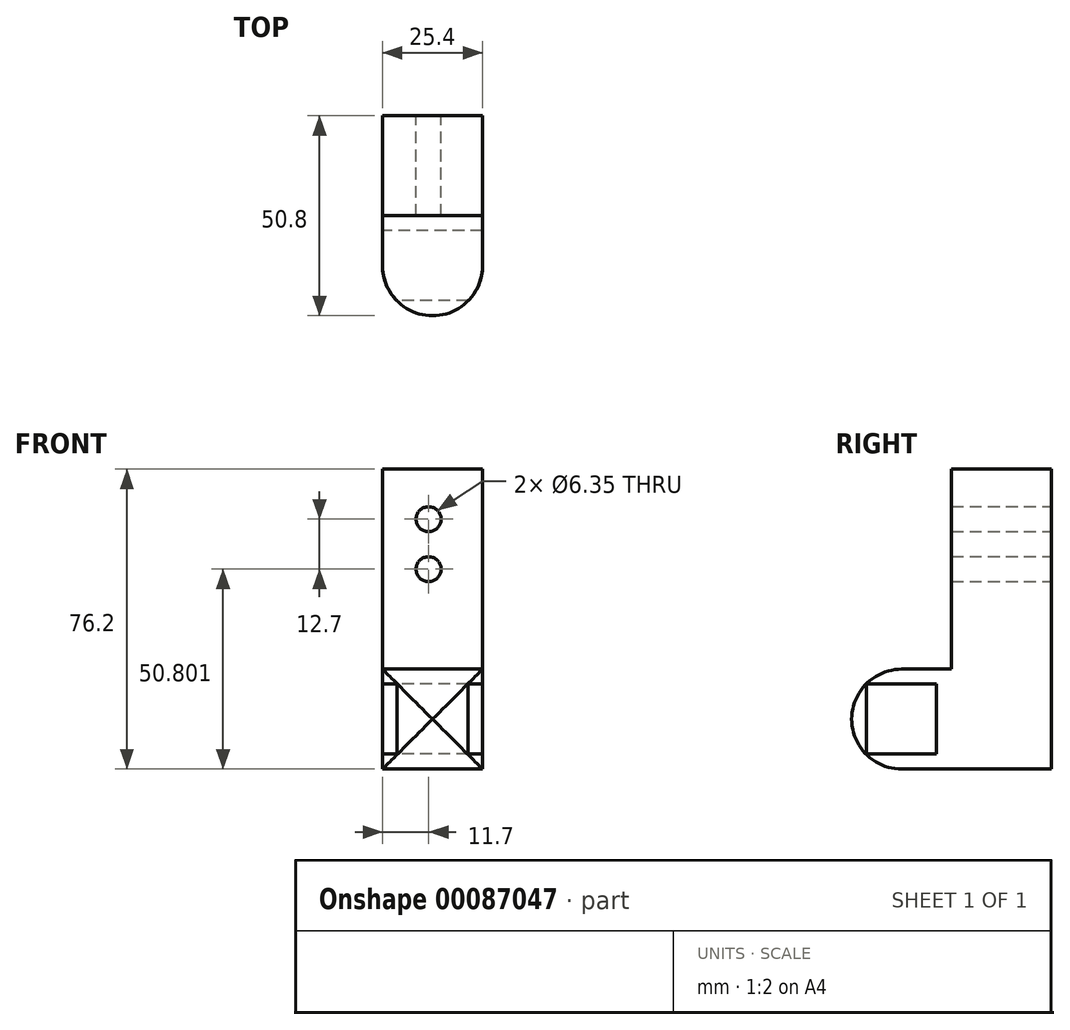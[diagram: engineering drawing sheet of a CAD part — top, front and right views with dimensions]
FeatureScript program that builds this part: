
annotation { "Feature Type Name" : "Feature", "Feature Type Description" : "" }
export const myFeature = defineFeature(function(context is Context, id is Id, definition is map)
    precondition{}
    {
        {
            var Q0;
            Q0=qCreatedBy(makeId("Front.planeOp"),FACE);
            var sketch = newSketch(context, id + "F0", { "sketchPlane" : qUnion([Q0])});
            skLineSegment(sketch, "E0.bottom", {"start": v(-11.7, 54.66) * mm, "end": v(13.7, 54.66) * mm});
            skLineSegment(sketch, "E0.top", {"start": v(-11.7, -21.54) * mm, "end": v(13.7, -21.54) * mm});
            skLineSegment(sketch, "E0.left", {"start": v(-11.7, 54.66) * mm, "end": v(-11.7, -21.54) * mm});
            skLineSegment(sketch, "E0.right", {"start": v(13.7, 54.66) * mm, "end": v(13.7, -21.54) * mm});
            skCircle(sketch, "E1", {"center": v(0, 41.96) * mm, "radius": 3.18 * mm});
            skCircle(sketch, "E2", {"center": v(0, 29.26) * mm, "radius": 3.18 * mm});
            skSolve(sketch);
        }
        {
            var Q0;
            Q0=makeQuery(id+"F0.imprint","IMPRINT",FACE,{"disambiguationData":[TD([[makeQuery(id+"F0.imprint","IMPRINT",EDGE,{"derivedFrom":sQuery(id+"F0.wireOp",EDGE,"E0.bottom")}),-1.0]])]});
            extrude(context, id + "F1", {"entities" : qUnion([Q0]), "depth" : 25.4 * mm});
        }
        {
            var Q0;
            Q0=makeQuery(id+"F1.opExtrude","CAP_FACE",FACE,{"disambiguationData":[OSD([sQuery(id+"F0.wireOp",EDGE,"E0.bottom"),sQuery(id+"F0.wireOp",EDGE,"E0.top"),sQuery(id+"F0.wireOp",EDGE,"E0.left"),sQuery(id+"F0.wireOp",EDGE,"E0.right"),sQuery(id+"F0.wireOp",EDGE,"E1"),sQuery(id+"F0.wireOp",EDGE,"E2")])],"isStart":false});
            var sketch = newSketch(context, id + "F2", { "sketchPlane" : qUnion([Q0])});
            skLineSegment(sketch, "E3.bottom", {"start": v(-11.7, 3.86) * mm, "end": v(13.7, 3.86) * mm});
            skLineSegment(sketch, "E3.top", {"start": v(-11.7, -21.54) * mm, "end": v(13.7, -21.54) * mm});
            skLineSegment(sketch, "E3.left", {"start": v(-11.7, 3.86) * mm, "end": v(-11.7, -21.54) * mm});
            skLineSegment(sketch, "E3.right", {"start": v(13.7, 3.86) * mm, "end": v(13.7, -21.54) * mm});
            skSolve(sketch);
        }
        {
            var Q0;
            Q0=makeQuery(id+"F2.imprint","IMPRINT",FACE,{"disambiguationData":[TD([[makeQuery(id+"F2.imprint","IMPRINT",EDGE,{"derivedFrom":sQuery(id+"F2.wireOp",EDGE,"E3.bottom")}),-1.0]])]});
            extrude(context, id + "F3", {"entities" : qUnion([Q0]), "operationType" : NewBodyOperationType.ADD, "depth" : 25.4 * mm});
        }
        {
            var Q0;
            Q0=makeQuery(id+"F3.opExtrude","SWEPT_FACE",FACE,{"disambiguationData":[OSD([sQuery(id+"F2.wireOp",EDGE,"E3.left")])]});
            var sketch = newSketch(context, id + "F4", { "sketchPlane" : qUnion([Q0])});
            skLineSegment(sketch, "E4.bottom", {"start": v(29.21, 0.05) * mm, "end": v(47, 0.05) * mm});
            skLineSegment(sketch, "E4.top", {"start": v(29.21, -17.73) * mm, "end": v(47, -17.73) * mm});
            skLineSegment(sketch, "E4.left", {"start": v(29.21, 0.05) * mm, "end": v(29.21, -17.73) * mm});
            skLineSegment(sketch, "E4.right", {"start": v(47, 0.05) * mm, "end": v(47, -17.73) * mm});
            skSolve(sketch);
        }
        {
            var Q0;
            Q0=makeQuery(id+"F4.imprint","IMPRINT",FACE,{"disambiguationData":[TD([[makeQuery(id+"F4.imprint","IMPRINT",EDGE,{"derivedFrom":sQuery(id+"F4.wireOp",EDGE,"E4.bottom")}),-1.0]])]});
            extrude(context, id + "F5", {"entities" : qUnion([Q0]), "operationType" : NewBodyOperationType.REMOVE, "endBound" : BoundingType.SYMMETRIC, "oppositeDirection" : true, "depth" : 127 * mm});
        }
        {
            var Q0;
            Q0=makeQuery(id+"F3.opExtrude","CAP_EDGE",EDGE,{"disambiguationData":[OSD([sQuery(id+"F2.wireOp",EDGE,"E3.bottom")])],"isStart":false});
            var Q1;
            Q1=makeQuery(id+"F3.opExtrude","CAP_FACE",FACE,{"disambiguationData":[OSD([sQuery(id+"F2.wireOp",EDGE,"E3.bottom"),sQuery(id+"F2.wireOp",EDGE,"E3.top"),sQuery(id+"F2.wireOp",EDGE,"E3.left"),sQuery(id+"F2.wireOp",EDGE,"E3.right")])],"isStart":false});
            fillet(context, id + "F6", {"entities" : qUnion([Q0, Q1]), "radius" : 12.7 * mm, "tangentPropagation" : true, "allowEdgeOverflow" : false});
        }
    });
